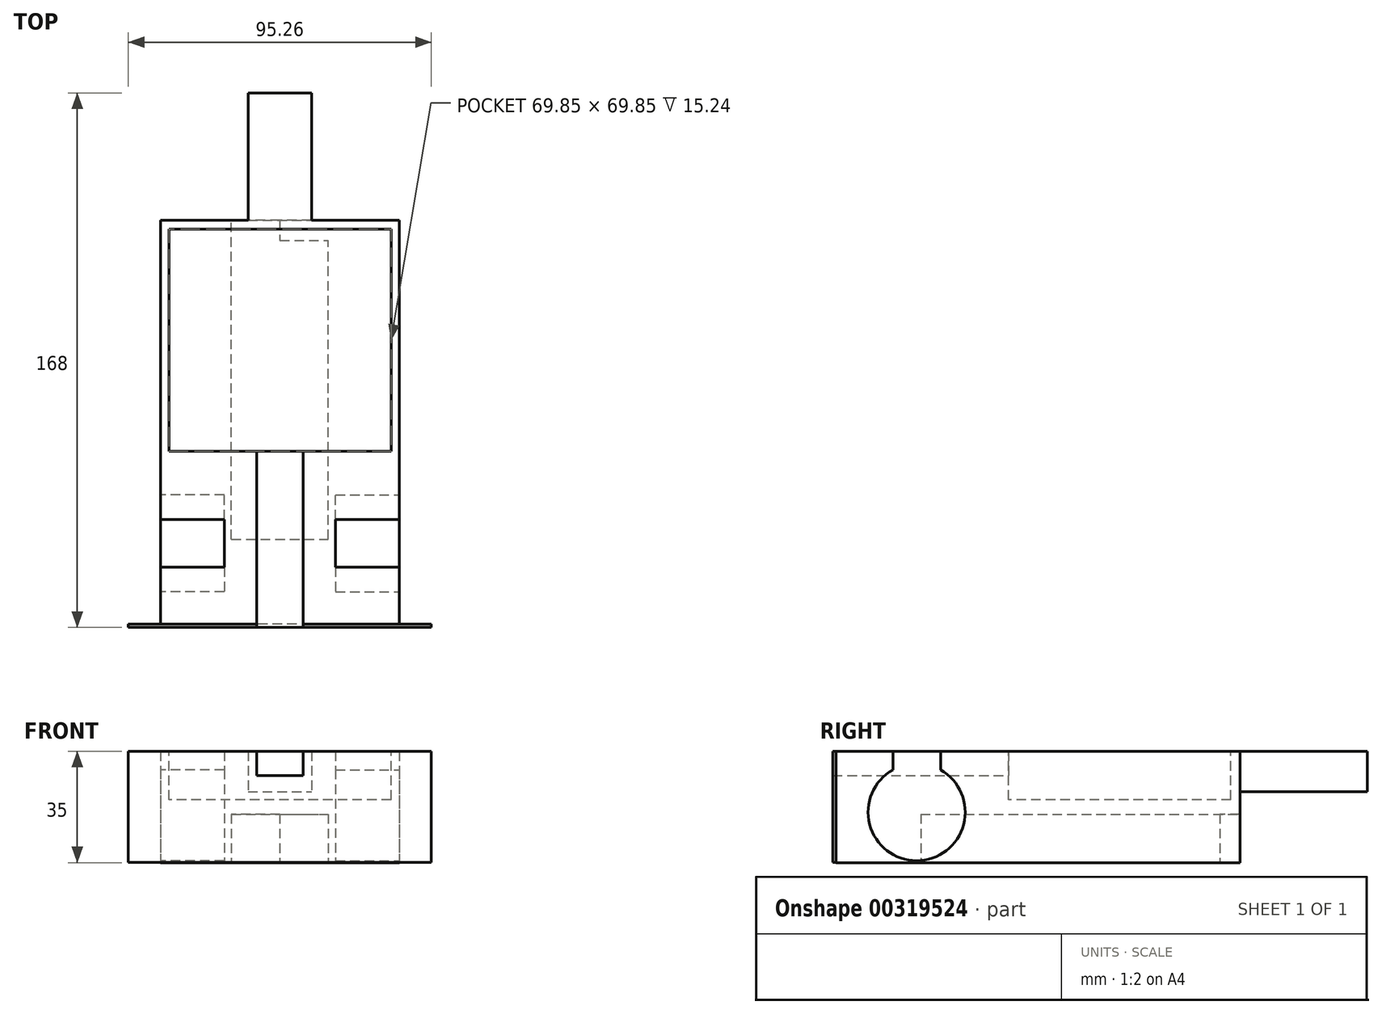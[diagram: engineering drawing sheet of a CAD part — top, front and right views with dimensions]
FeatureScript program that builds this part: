
annotation { "Feature Type Name" : "Feature", "Feature Type Description" : "" }
export const myFeature = defineFeature(function(context is Context, id is Id, definition is map)
    precondition{}
    {
        {
            var Q0;
            Q0=qCreatedBy(makeId("Front.planeOp"),FACE);
            var sketch = newSketch(context, id + "F0", { "sketchPlane" : qUnion([Q0])});
            skLineSegment(sketch, "E0.bottom", {"start": v(37.5, 17.5) * mm, "end": v(-37.5, 17.5) * mm});
            skLineSegment(sketch, "E0.top", {"start": v(37.5, -17.5) * mm, "end": v(-37.5, -17.5) * mm});
            skLineSegment(sketch, "E0.left", {"start": v(37.5, 17.5) * mm, "end": v(37.5, -17.5) * mm});
            skLineSegment(sketch, "E0.right", {"start": v(-37.5, 17.5) * mm, "end": v(-37.5, -17.5) * mm});
            skPoint(sketch, "E0.middle", {"position": v(0, 0) * mm});
            skSolve(sketch);
        }
        {
            var Q0;
            Q0=makeQuery(id+"F0.imprint","IMPRINT",FACE,{"disambiguationData":[TD([[makeQuery(id+"F0.imprint","IMPRINT",EDGE,{"derivedFrom":sQuery(id+"F0.wireOp",EDGE,"E0.bottom")}),1.0]])]});
            extrude(context, id + "F1", {"entities" : qUnion([Q0]), "oppositeDirection" : true, "depth" : 127 * mm});
        }
        {
            var Q0;
            Q0=makeQuery(id+"F1.opExtrude","SWEPT_FACE",FACE,{"disambiguationData":[OSD([sQuery(id+"F0.wireOp",EDGE,"E0.left")])]});
            var sketch = newSketch(context, id + "F2", { "sketchPlane" : qUnion([Q0])});
            skCircle(sketch, "E1", {"center": v(25.4, -1.63) * mm, "radius": 15.27 * mm});
            skPoint(sketch, "E1.first.point", {"position": v(25.4, 13.64) * mm});
            skPoint(sketch, "E1.second.point", {"position": v(40.59, 0) * mm});
            skPoint(sketch, "E1.third.point", {"position": v(29.41, -16.36) * mm});
            skLineSegment(sketch, "E2.bottom", {"start": v(32.9, 17.5) * mm, "end": v(17.9, 17.5) * mm});
            skLineSegment(sketch, "E2.top", {"start": v(32.9, 9.79) * mm, "end": v(17.9, 9.79) * mm});
            skLineSegment(sketch, "E2.left", {"start": v(32.9, 17.5) * mm, "end": v(32.9, 9.79) * mm});
            skLineSegment(sketch, "E2.right", {"start": v(17.9, 17.5) * mm, "end": v(17.9, 9.79) * mm});
            skSolve(sketch);
        }
        {
            var Q0;
            {var subQ5=sQuery(id+"F2.wireOp",EDGE,"E2.bottom");Q0=makeQuery(id+"F2.imprint","IMPRINT",FACE,{"disambiguationData":[TD([[makeQuery(id+"F2.imprint","IMPRINT",EDGE,{"derivedFrom":subQ5}),1.0]])]});}
            var Q1;
            {var subQ5=sQuery(id+"F2.wireOp",EDGE,"E2.top");Q1=makeQuery(id+"F2.imprint","IMPRINT",FACE,{"disambiguationData":[TD([[makeQuery(id+"F2.imprint","IMPRINT",EDGE,{"derivedFrom":subQ5}),-1.0]])]});}
            var Q2;
            {var subQ5=sQuery(id+"F2.wireOp",EDGE,"E2.top");Q2=makeQuery(id+"F2.imprint","IMPRINT",FACE,{"disambiguationData":[TD([[makeQuery(id+"F2.imprint","IMPRINT",EDGE,{"derivedFrom":subQ5}),1.0]])]});}
            extrude(context, id + "F3", {"entities" : qUnion([Q0, Q1, Q2]), "operationType" : NewBodyOperationType.REMOVE, "oppositeDirection" : true, "depth" : 20 * mm});
        }
        {
            var Q0;
            Q0=makeQuery(id+"F1.opExtrude","SWEPT_BODY",BODY,{"disambiguationData":[OSD([sQuery(id+"F0.wireOp",EDGE,"E0.bottom"),sQuery(id+"F0.wireOp",EDGE,"E0.top"),sQuery(id+"F0.wireOp",EDGE,"E0.left"),sQuery(id+"F0.wireOp",EDGE,"E0.right")])]});
            var Q1;
            Q1=qCreatedBy(makeId("Right.planeOp"),FACE);
            mirror(context, id + "F4", {"operationType" : NewBodyOperationType.INTERSECT, "entities" : qUnion([Q0]), "mirrorPlane" : qUnion([Q1])});
        }
        {
            var Q0;
            Q0=makeQuery(id+"F1.opExtrude","CAP_FACE",FACE,{"disambiguationData":[OSD([sQuery(id+"F0.wireOp",EDGE,"E0.bottom"),sQuery(id+"F0.wireOp",EDGE,"E0.top"),sQuery(id+"F0.wireOp",EDGE,"E0.left"),sQuery(id+"F0.wireOp",EDGE,"E0.right")])],"isStart":false});
            var sketch = newSketch(context, id + "F5", { "sketchPlane" : qUnion([Q0])});
            skLineSegment(sketch, "E3.left", {"start": v(10, 17.5) * mm, "end": v(10, 4.8) * mm});
            skPoint(sketch, "E3.middle", {"position": v(0, 0) * mm});
            skLineSegment(sketch, "E4.bottom", {"start": v(10, 17.5) * mm, "end": v(-9.99, 17.5) * mm});
            skLineSegment(sketch, "E4.top", {"start": v(10, 4.8) * mm, "end": v(-9.99, 4.8) * mm});
            skLineSegment(sketch, "E4.right", {"start": v(-9.99, 17.5) * mm, "end": v(-9.99, 4.8) * mm});
            skSolve(sketch);
        }
        {
            var Q0;
            Q0=makeQuery(id+"F5.imprint","IMPRINT",FACE,{"disambiguationData":[TD([[makeQuery(id+"F5.imprint","IMPRINT",EDGE,{"derivedFrom":sQuery(id+"F5.wireOp",EDGE,"E3.bottom")}),-1.0]])]});
            var Q1;
            Q1=makeQuery(id+"F5.imprint","IMPRINT",FACE,{"disambiguationData":[TD([[makeQuery(id+"F5.imprint","IMPRINT",EDGE,{"derivedFrom":sQuery(id+"F5.wireOp",EDGE,"E4.bottom")}),-1.0]])]});
            extrude(context, id + "F6", {"entities" : qUnion([Q0, Q1]), "operationType" : NewBodyOperationType.ADD, "depth" : 40 * mm});
        }
        {
            var Q0;
            Q0=makeQuery(id+"F6.boolean.opBoolean","MERGE",FACE,{"derivedFrom":[makeQuery(id+"F1.opExtrude","SWEPT_FACE",FACE,{"disambiguationData":[OSD([sQuery(id+"F0.wireOp",EDGE,"E0.bottom")])]}),makeQuery(id+"F6.opExtrude","SWEPT_FACE",FACE,{"disambiguationData":[OSD([sQuery(id+"F5.wireOp",EDGE,"E4.bottom")])]})]});
            var sketch = newSketch(context, id + "F7", { "sketchPlane" : qUnion([Q0])});
            skLineSegment(sketch, "E5.bottom", {"start": v(35, 124.17) * mm, "end": v(-34.85, 124.17) * mm});
            skLineSegment(sketch, "E5.top", {"start": v(35, 54.32) * mm, "end": v(-34.85, 54.32) * mm});
            skLineSegment(sketch, "E5.left", {"start": v(35, 124.17) * mm, "end": v(35, 54.32) * mm});
            skLineSegment(sketch, "E5.right", {"start": v(-34.85, 124.17) * mm, "end": v(-34.85, 54.32) * mm});
            skSolve(sketch);
        }
        {
            var Q0;
            Q0=makeQuery(id+"F7.imprint","IMPRINT",FACE,{"disambiguationData":[TD([[makeQuery(id+"F7.imprint","IMPRINT",EDGE,{"derivedFrom":sQuery(id+"F7.wireOp",EDGE,"2GYMT8Zs-Esro-Z6J7-4q6w-Ump0UPWscq1a.bottom")}),-1.0]])]});
            var Q1;
            Q1=makeQuery(id+"F7.imprint","IMPRINT",FACE,{"disambiguationData":[TD([[makeQuery(id+"F7.imprint","IMPRINT",EDGE,{"derivedFrom":sQuery(id+"F7.wireOp",EDGE,"E5.bottom")}),1.0]])]});
            extrude(context, id + "F8", {"entities" : qUnion([Q0, Q1]), "operationType" : NewBodyOperationType.REMOVE, "oppositeDirection" : true, "depth" : 15.24 * mm});
        }
        {
            var Q0;
            Q0=qCreatedBy(makeId("Front.planeOp"),FACE);
            var sketch = newSketch(context, id + "F9", { "sketchPlane" : qUnion([Q0])});
            skLineSegment(sketch, "E6.bottom", {"start": v(47.63, -17.48) * mm, "end": v(-47.63, -17.48) * mm});
            skLineSegment(sketch, "E6.top", {"start": v(47.63, 17.48) * mm, "end": v(-47.63, 17.48) * mm});
            skLineSegment(sketch, "E6.left", {"start": v(47.63, -17.48) * mm, "end": v(47.63, 17.48) * mm});
            skLineSegment(sketch, "E6.right", {"start": v(-47.63, -17.48) * mm, "end": v(-47.63, 17.48) * mm});
            skPoint(sketch, "E6.middle", {"position": v(0, 0) * mm});
            skSolve(sketch);
        }
        {
            var Q0;
            Q0=makeQuery(id+"F9.imprint","IMPRINT",FACE,{"disambiguationData":[TD([[makeQuery(id+"F9.imprint","IMPRINT",EDGE,{"derivedFrom":sQuery(id+"F9.wireOp",EDGE,"E6.bottom")}),-1.0]])]});
            extrude(context, id + "F10", {"entities" : qUnion([Q0]), "operationType" : NewBodyOperationType.ADD, "depth" : 1 * mm});
        }
        {
            var Q0;
            Q0=makeQuery(id+"F6.boolean.opBoolean","MERGE",FACE,{"derivedFrom":[makeQuery(id+"F1.opExtrude","SWEPT_FACE",FACE,{"disambiguationData":[OSD([sQuery(id+"F0.wireOp",EDGE,"E0.bottom")])]}),makeQuery(id+"F6.opExtrude","SWEPT_FACE",FACE,{"disambiguationData":[OSD([sQuery(id+"F5.wireOp",EDGE,"E4.bottom")])]})]});
            var sketch = newSketch(context, id + "F11", { "sketchPlane" : qUnion([Q0])});
            skLineSegment(sketch, "E7.bottom", {"start": v(-7.26, -1) * mm, "end": v(7.37, -1) * mm});
            skLineSegment(sketch, "E7.top", {"start": v(-7.26, 56.15) * mm, "end": v(7.37, 56.15) * mm});
            skLineSegment(sketch, "E7.left", {"start": v(-7.26, -1) * mm, "end": v(-7.26, 56.15) * mm});
            skLineSegment(sketch, "E7.right", {"start": v(7.37, -1) * mm, "end": v(7.37, 56.15) * mm});
            skSolve(sketch);
        }
        {
            var Q0;
            Q0=qSketchRegion(id+"F11",true);
            extrude(context, id + "F12", {"entities" : qUnion([Q0]), "operationType" : NewBodyOperationType.REMOVE, "oppositeDirection" : true, "depth" : 7.62 * mm});
        }
        {
            var Q0;
            Q0=makeQuery(id+"F1.opExtrude","SWEPT_FACE",FACE,{"disambiguationData":[OSD([sQuery(id+"F0.wireOp",EDGE,"E0.top")])]});
            var sketch = newSketch(context, id + "F13", { "sketchPlane" : qUnion([Q0])});
            skLineSegment(sketch, "E8.bottom", {"start": v(-15.24, -26.67) * mm, "end": v(15.24, -26.67) * mm});
            skLineSegment(sketch, "E8.top", {"start": v(-15.24, -120.65) * mm, "end": v(15.24, -120.65) * mm});
            skLineSegment(sketch, "E8.left", {"start": v(-15.24, -26.67) * mm, "end": v(-15.24, -120.65) * mm});
            skLineSegment(sketch, "E8.right", {"start": v(15.24, -26.67) * mm, "end": v(15.24, -120.65) * mm});
            skSolve(sketch);
        }
        {
            var Q0;
            Q0=makeQuery(id+"F13.imprint","IMPRINT",FACE,{"disambiguationData":[TD([[makeQuery(id+"F13.imprint","IMPRINT",EDGE,{"derivedFrom":sQuery(id+"F13.wireOp",EDGE,"E8.bottom")}),-1.0]])]});
            extrude(context, id + "F14", {"entities" : qUnion([Q0]), "operationType" : NewBodyOperationType.REMOVE, "oppositeDirection" : true, "depth" : 15.24 * mm});
        }
        {
            var Q0;
            Q0=makeQuery(id+"F1.opExtrude","SWEPT_FACE",FACE,{"disambiguationData":[OSD([sQuery(id+"F0.wireOp",EDGE,"E0.top")])]});
            var sketch = newSketch(context, id + "F15", { "sketchPlane" : qUnion([Q0])});
            skLineSegment(sketch, "E9.bottom", {"start": v(0, -127) * mm, "end": v(-15.24, -127) * mm});
            skLineSegment(sketch, "E9.top", {"start": v(0, -120.65) * mm, "end": v(-15.24, -120.65) * mm});
            skLineSegment(sketch, "E9.left", {"start": v(0, -127) * mm, "end": v(0, -120.65) * mm});
            skLineSegment(sketch, "E9.right", {"start": v(-15.24, -127) * mm, "end": v(-15.24, -120.65) * mm});
            skSolve(sketch);
        }
        {
            var Q0;
            Q0=makeQuery(id+"F15.imprint","IMPRINT",FACE,{"disambiguationData":[TD([[makeQuery(id+"F15.imprint","IMPRINT",EDGE,{"derivedFrom":sQuery(id+"F15.wireOp",EDGE,"E9.bottom")}),-1.0]])]});
            extrude(context, id + "F16", {"entities" : qUnion([Q0]), "operationType" : NewBodyOperationType.REMOVE, "oppositeDirection" : true, "depth" : 15.24 * mm});
        }
    });
